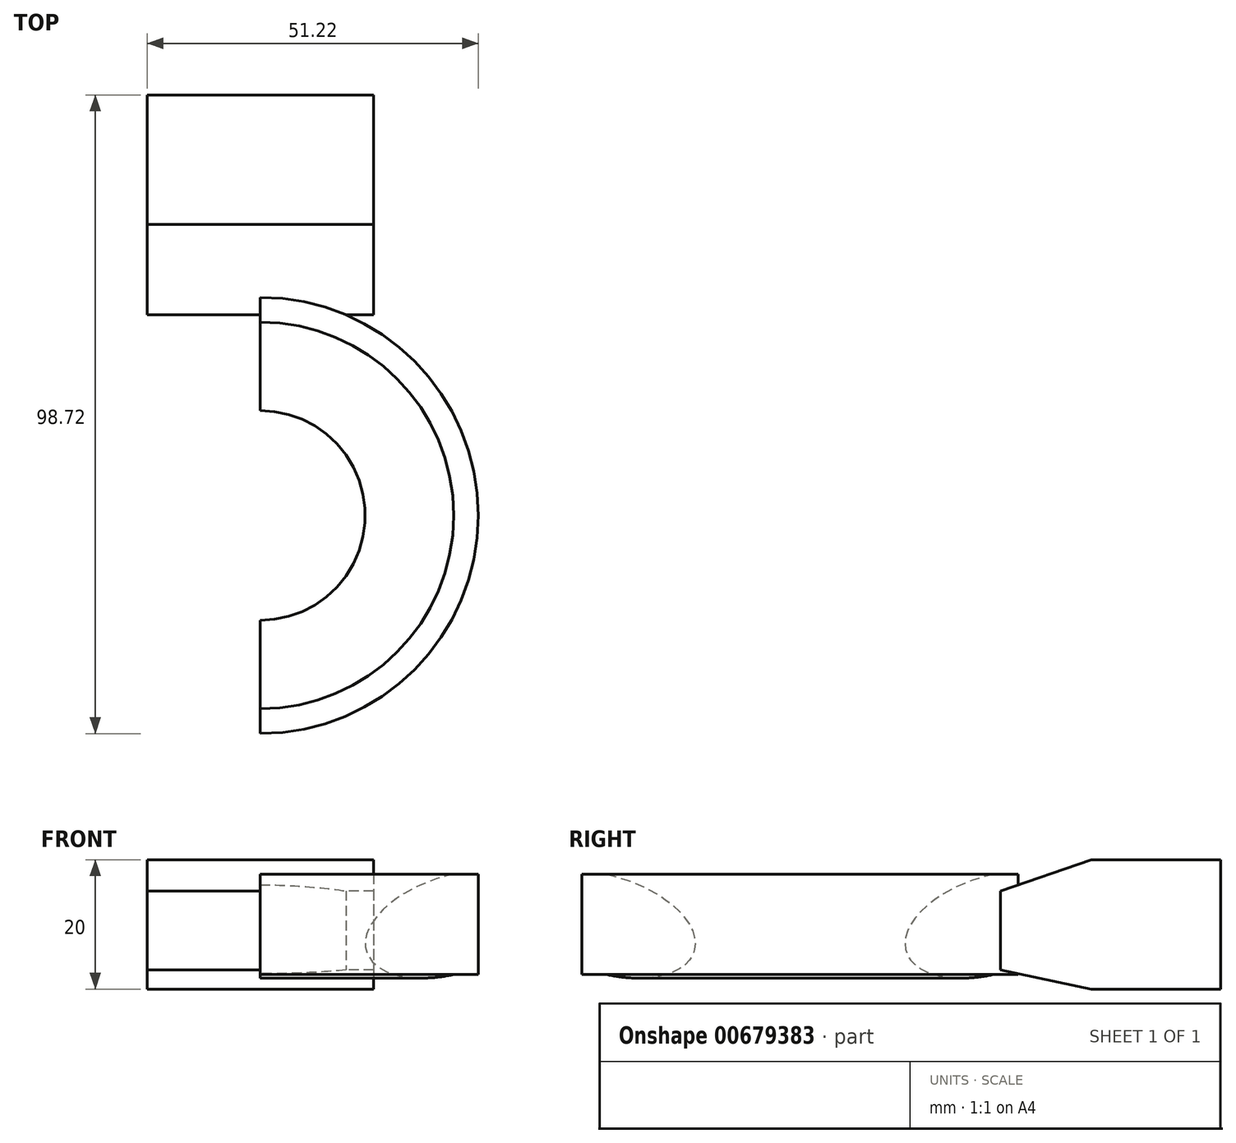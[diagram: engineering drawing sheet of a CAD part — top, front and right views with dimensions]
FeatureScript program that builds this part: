
annotation { "Feature Type Name" : "Feature", "Feature Type Description" : "" }
export const myFeature = defineFeature(function(context is Context, id is Id, definition is map)
    precondition{}
    {
        {
            var Q0;
            Q0=qCreatedBy(makeId("Top.planeOp"),FACE);
            var sketch = newSketch(context, id + "F0", { "sketchPlane" : qUnion([Q0])});
            skArc(sketch, "E0", {"start": v(0, -30) * mm, "mid": v(30, 0) * mm, "end": v(0, 30) * mm});
            skSolve(sketch);
        }
        {
            var Q0;
            Q0=qCreatedBy(makeId("Top.planeOp"),FACE);
            var sketch = newSketch(context, id + "F1", { "sketchPlane" : qUnion([Q0])});
            skLineSegment(sketch, "E1.bottom", {"start": v(-17.5, 45) * mm, "end": v(17.5, 45) * mm});
            skLineSegment(sketch, "E1.top", {"start": v(-17.5, 65) * mm, "end": v(17.5, 65) * mm});
            skLineSegment(sketch, "E1.left", {"start": v(-17.5, 45) * mm, "end": v(-17.5, 65) * mm});
            skLineSegment(sketch, "E1.right", {"start": v(17.5, 45) * mm, "end": v(17.5, 65) * mm});
            skSolve(sketch);
        }
        {
            var Q0;
            Q0 = qSketchRegion(id + "F1", true);
            extrude(context, id + "F2", {"entities" : qUnion([Q0]), "depth" : 20 * mm, "offsetDistance" : 25 * mm});
        }
        {
            var Q0;
            Q0=makeQuery(id+"F2.opExtrude","SWEPT_BODY",BODY,{"disambiguationData":[OSD([sQuery(id+"F1.wireOp",EDGE,"E1.bottom"),sQuery(id+"F1.wireOp",EDGE,"E1.top"),sQuery(id+"F1.wireOp",EDGE,"E1.left"),sQuery(id+"F1.wireOp",EDGE,"E1.right")])]});
            transform(context, id + "F3", {"entities" : qUnion([Q0]), "transformType" : TransformType.TRANSLATION_3D, "dx" : 0 * mm, "dy" : 0 * mm, "dz" : -10 * mm, "makeCopy" : false});
        }
        {
            var Q0;
            Q0=makeQuery(id+"F2.opExtrude","SWEPT_FACE",FACE,{"disambiguationData":[OSD([sQuery(id+"F1.wireOp",EDGE,"E1.left")])]});
            var sketch = newSketch(context, id + "F4", { "sketchPlane" : qUnion([Q0])});
            skLineSegment(sketch, "E2", {"start": v(-45, 10) * mm, "end": v(-31, 5.17) * mm});
            skLineSegment(sketch, "E3", {"start": v(-31, 5.17) * mm, "end": v(-31, -7.06) * mm});
            skLineSegment(sketch, "E4", {"start": v(-31, -7.06) * mm, "end": v(-45, -10) * mm});
            skSolve(sketch);
        }
        {
            var Q0;
            Q0=makeQuery(id+"F4.imprint","IMPRINT",FACE,{"disambiguationData":[TD([[makeQuery(id+"F4.imprint","IMPRINT",EDGE,{"derivedFrom":sQuery(id+"F4.wireOp",EDGE,"E2")}),-1.0]])]});
            extrude(context, id + "F5", {"entities" : qUnion([Q0]), "oppositeDirection" : true, "depth" : 35 * mm, "offsetDistance" : 25 * mm});
        }
        {
            var Q0;
            Q0=qCreatedBy(makeId("Right.planeOp"),FACE);
            var sketch = newSketch(context, id + "F6", { "sketchPlane" : qUnion([Q0])});
            skEllipticalArc(sketch, "E5", {});
            skLineSegment(sketch, "E6", {"start": v(29.9, 7.75) * mm, "end": v(29.9, -7.75) * mm, "construction": true});
            skLineSegment(sketch, "E7", {"start": v(29.9, 7.75) * mm, "end": v(33.72, 7.75) * mm});
            skLineSegment(sketch, "E8", {"start": v(33.72, 7.75) * mm, "end": v(33.72, -7.75) * mm});
            skLineSegment(sketch, "E9", {"start": v(33.72, -7.75) * mm, "end": v(29.9, -7.75) * mm});
            skLineSegment(sketch, "E10", {"start": v(31.64, -1.93) * mm, "end": v(30.5, -4.64) * mm});
            skPoint(sketch, "E11.visualSharp", {"position": v(32.45, 0) * mm});
            skArc(sketch, "E11.filletArc", {"start": v(31.64, -1.93) * mm, "mid": v(32.03, 0) * mm, "end": v(31.64, 1.93) * mm});
            skPoint(sketch, "E12.visualSharp", {"position": v(29.9, 6.11) * mm});
            skFitSpline(sketch, "E13.trimOffspring", {"points": [v(42.02, 2.86) * mm, v(41.9, 3.75) * mm, v(41.5, 4.55) * mm, v(40.81, 5.2) * mm, v(40.02, 5.67) * mm, v(39.07, 6.1) * mm, v(37.62, 6.5) * mm, v(35.87, 6.7) * mm, v(34.33, 6.71) * mm, v(32.73, 6.62) * mm, v(31.07, 6.38) * mm, v(29.4, 6) * mm, v(28.13, 5.64) * mm, v(26.9, 5.22) * mm, v(25.3, 4.58) * mm, v(23.79, 3.83) * mm, v(22.42, 3) * mm, v(21.16, 2.12) * mm, v(19.83, 0.96) * mm, v(18.87, -0.2) * mm, v(18.33, -1.1) * mm, v(17.95, -1.93) * mm, v(17.76, -2.86) * mm, v(17.87, -3.75) * mm, v(18.29, -4.55) * mm, v(18.97, -5.2) * mm, v(19.76, -5.67) * mm, v(20.7, -6.1) * mm, v(22.16, -6.5) * mm, v(23.91, -6.7) * mm, v(25.45, -6.71) * mm, v(27.05, -6.62) * mm, v(28.71, -6.38) * mm, v(30.4, -6) * mm, v(31.65, -5.64) * mm, v(32.9, -5.22) * mm, v(34.5, -4.58) * mm, v(36, -3.83) * mm, v(37.36, -3) * mm, v(38.62, -2.12) * mm, v(39.95, -0.96) * mm, v(40.91, 0.2) * mm, v(41.45, 1.1) * mm, v(41.83, 1.93) * mm, v(42.02, 2.86) * mm, v(41.9, 3.75) * mm, v(41.5, 4.55) * mm]});
            skLineSegment(sketch, "E14", {"start": v(30.93, 3.64) * mm, "end": v(31.64, 1.93) * mm});
            skArc(sketch, "E15.filletArc", {"start": v(30.93, 3.64) * mm, "mid": v(29.37, 5.22) * mm, "end": v(27.15, 5.3) * mm});
            skPoint(sketch, "E16.visualSharp", {"position": v(29.9, -6.11) * mm});
            skArc(sketch, "E16.filletArc", {"start": v(28.21, -6.44) * mm, "mid": v(29.6, -5.84) * mm, "end": v(30.5, -4.64) * mm});
            const initialGuessF6  = {"E5": [0.029891112819313996, 0, 0.9546425080054789, 0.29775439863922915, 0.014137182707815481, 0.0075, 1.406813481204943, 4.548406134794735]};
            skSetInitialGuess(sketch, initialGuessF6);
            skSolve(sketch);
        }
        {
            var Q0;
            Q0=makeQuery(id+"F6.imprint","IMPRINT",FACE,{"disambiguationData":[TD([[makeQuery(id+"F6.imprint","IMPRINT",EDGE,{"derivedFrom":sQuery(id+"F6.wireOp",EDGE,"E5")}),1.0]])]});
            var Q1;
            Q1=sQuery(id+"F0.wireOp",EDGE,"E0");
            sweep(context, id + "F7", {"profiles" : qUnion([Q0]), "path" : qUnion([Q1])});
        }
        {
            var Q0;
            Q0=makeQuery(id+"F5.opExtrude","SWEPT_BODY",BODY,{"disambiguationData":[OSD([sQuery(id+"F1.wireOp",EDGE,"E1.bottom"),sQuery(id+"F1.wireOp",EDGE,"E1.left"),sQuery(id+"F4.wireOp",EDGE,"E2"),sQuery(id+"F4.wireOp",EDGE,"E3"),sQuery(id+"F4.wireOp",EDGE,"E4")])]});
            var Q1;
            Q1=qCreatedBy(makeId("Right.planeOp"),FACE);
            mirror(context, id + "F8", {"operationType" : NewBodyOperationType.ADD, "entities" : qUnion([Q0]), "mirrorPlane" : qUnion([Q1])});
        }
    });
